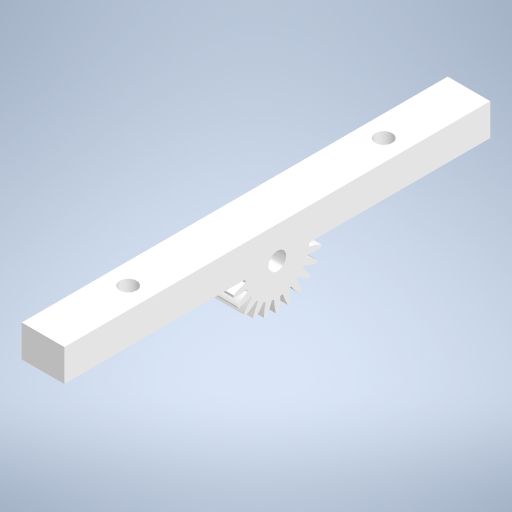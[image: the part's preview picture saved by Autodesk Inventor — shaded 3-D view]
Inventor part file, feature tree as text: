
AUTODESK INVENTOR PART (.ipt)
format: ipt  version: 2024 (Build 280153000, 153)  size: 406,528 bytes
history: native  units: mm
features: sketch x3, extrude x2, other x1, hole x1
ambient origin geometry x8: Origin, YZ Plane, XZ Plane, XY Plane, X Axis, Y Axis, Z Axis, Center Point
bodies: Body1 (feature_tree)
feature tree (7):
  other  "솔리드1"
  extrude  "돌출1"  Depth=4.2mm
  hole  "구멍2"  [1 undecoded]
  extrude  "돌출3"  Depth=100.0mm
  sketch  "스케치1"
  sketch  "스케치4"
  sketch  "스케치5"
note: 1 required parameter value undecoded (feature->parameter linkage not recoverable at this tier; creation-order binding heuristic only, values carry confidence <= 0.55)
